# Revit family: Rohrschelle Sigma, M 8, Gummi schwarz
name_source: partatom
category: HLS-Bauteile
revit_build: Autodesk Revit 2017 (Build: 20190507_1515(x64)
units: mm (PartAtom-declared; Revit-internal decimal feet)

## family parameters
Arbeitsebenenbasiert = Ja
Beim Laden mit Abzugskörper schneiden = Nein
Bemaßung runder Anschluss = Durchmesser verwenden
Gemeinsam genutzt = Ja
Immer vertikal = Nein
Raumberechnungspunkt = Nein
Teiletyp = Normal

## types (10) — shared parameters
Anschluss = M8
Anschlußhöhe = 12 mm
Bauart = einteilig
Baustoffklasse = B2
DS = 3 mm  [stored 0.00984252 ft]
DVS = 5 mm  [stored 0.0164042 ft]
Dämmstärke = 3 mm  [stored 0.00984252 ft]
Fabrikat = MEFA
Farbe Schalldämmeinlage = schwarz
Firma = MEFA Befestigungs- und Montagesysteme GmbH
HGA = 8 mm  [stored 0.0262467 ft]
MB = 20 mm  [stored 0.0656168 ft]
Material = Stahl
Material Schalldämmeinlage = EPDM
Materialname = DC01-A, DD11
Mengeneinheit = St
Oberflaeche = galvanisch verzinkt
Schalldämmeinlage = Gummi
Verschluss = Sigma Sicherheits-Schnellverschluss
Verschluss-Schraube = M5
Vorgabe-Ansicht = 1219 mm
max. Temperaturbeständigkeit = 100 °C
max. zul. Last horizontal = 0.00 kN
max. zul. Last vertikal = 0.00 kN
zero-valued in all types: Nennweite DN Rohr, Rohraußendurchmesser, Stärke Material

## per-type parameters (varying)
- Sigma, Ø  6- 10, M 8, Gummi schwarz: A=12 mm  [stored 0.0393701 ft]; Artikelnummer=14510150; B=33 mm  [stored 0.108268 ft]; Breite=33 mm  [stored 0.108268 ft]; D=10 mm  [stored 0.0328084 ft]; D0=16 mm  [stored 0.0524934 ft]; DF1=17 mm; DF2=6 mm  [stored 0.019685 ft]; Dmax=10 mm  [stored 0.0328084 ft]; EAN=4250928454645; Gewicht=0.02 kg; Gewicht pro Bauteil=0.02 kg; H=26 mm  [stored 0.0853018 ft]; Kurztext1=Rohrschelle Sigma 20x1,0; Kurztext2=6 - 10 mm M8 EPDM; MD=1 mm  [stored 0.00328084 ft]; Materialmaße=20x1,0 mm; R=8 mm  [stored 0.0262467 ft]; RM=9 mm  [stored 0.0295276 ft]; Rohraußendurchmesser Zoll=Zoll; max. Höhe=27 mm  [stored 0.0885827 ft]; max. Rohraußendurchmesser=10 mm  [stored 0.0328084 ft]; max. zul. Last=0.60 kN; min. Rohraußendurchmesser=6 mm  [stored 0.019685 ft]; vpe=100 St
- Sigma, Ø 12- 15, M 8, Gummi schwarz: A=12 mm  [stored 0.0393701 ft]; Artikelnummer=14510151; B=41 mm  [stored 0.134514 ft]; Breite=41 mm  [stored 0.134514 ft]; D=15 mm  [stored 0.0492126 ft]; D0=21 mm  [stored 0.0688976 ft]; DF1=19 mm  [stored 0.062336 ft]; DF2=7 mm  [stored 0.0229659 ft]; Dmax=15 mm  [stored 0.0492126 ft]; EAN=4250928432162; Gewicht=0.03 kg; Gewicht pro Bauteil=0.03 kg; H=31 mm  [stored 0.101706 ft]; Kurztext1=Rohrschelle Sigma 20x1,0; Kurztext2=12 - 15 mm M8 EPDM; MD=1 mm  [stored 0.00328084 ft]; Materialmaße=20x1,0 mm; R=11 mm; RM=12 mm  [stored 0.0393701 ft]; Rohraußendurchmesser Zoll=1/4 Zoll; max. Höhe=33 mm  [stored 0.108268 ft]; max. Rohraußendurchmesser=15 mm  [stored 0.0492126 ft]; max. zul. Last=0.60 kN; min. Rohraußendurchmesser=12 mm  [stored 0.0393701 ft]; vpe=100 St
- Sigma, Ø 16- 19, M 8, Gummi schwarz: A=12 mm  [stored 0.0393701 ft]; Artikelnummer=14510191; B=45 mm  [stored 0.147638 ft]; Breite=45 mm  [stored 0.147638 ft]; D=19 mm  [stored 0.062336 ft]; D0=25 mm  [stored 0.082021 ft]; DF1=19 mm  [stored 0.062336 ft]; DF2=7 mm  [stored 0.0229659 ft]; Dmax=19 mm  [stored 0.062336 ft]; EAN=4250928432179; Gewicht=0.03 kg; Gewicht pro Bauteil=0.03 kg; H=35 mm  [stored 0.114829 ft]; Kurztext1=Rohrschelle Sigma 20x1,0; Kurztext2=16 - 19 mm M8 EPDM; MD=1 mm  [stored 0.00328084 ft]; Materialmaße=20x1,0 mm; R=13 mm; RM=14 mm  [stored 0.0459318 ft]; Rohraußendurchmesser Zoll=3/8 Zoll; max. Höhe=37 mm  [stored 0.121391 ft]; max. Rohraußendurchmesser=19 mm  [stored 0.062336 ft]; max. zul. Last=0.60 kN; min. Rohraußendurchmesser=16 mm  [stored 0.0524934 ft]; vpe=100 St
- Sigma, Ø 25- 29, M 8, Gummi schwarz: A=12 mm  [stored 0.0393701 ft]; Artikelnummer=14510291; B=56 mm; Breite=56 mm; D=29 mm  [stored 0.0951444 ft]; D0=35 mm  [stored 0.114829 ft]; DF1=19 mm  [stored 0.062336 ft]; DF2=8 mm  [stored 0.0262467 ft]; Dmax=29 mm  [stored 0.0951444 ft]; EAN=4250928432193; Gewicht=0.04 kg; Gewicht pro Bauteil=0.04 kg; H=45 mm  [stored 0.147638 ft]; Kurztext1=Rohrschelle Sigma 20x1,0; Kurztext2=25 - 29 mm M8 EPDM; MD=1 mm  [stored 0.00328084 ft]; Materialmaße=20x1,0 mm; R=18 mm  [stored 0.0590551 ft]; RM=19 mm  [stored 0.062336 ft]; Rohraußendurchmesser Zoll=3/4 Zoll; max. Höhe=47 mm  [stored 0.154199 ft]; max. Rohraußendurchmesser=29 mm  [stored 0.0951444 ft]; max. zul. Last=0.60 kN; min. Rohraußendurchmesser=25 mm  [stored 0.082021 ft]; vpe=100 St
- Sigma, Ø 32- 35, M 8, Gummi schwarz: A=12 mm  [stored 0.0393701 ft]; Artikelnummer=14510351; B=62 mm; Breite=62 mm; D=35 mm  [stored 0.114829 ft]; D0=41 mm  [stored 0.134514 ft]; DF1=19 mm  [stored 0.062336 ft]; DF2=8 mm  [stored 0.0262467 ft]; Dmax=35 mm  [stored 0.114829 ft]; EAN=4250928432209; Gewicht=0.04 kg; Gewicht pro Bauteil=0.04 kg; H=51 mm; Kurztext1=Rohrschelle Sigma 20x1,0; Kurztext2=32 - 35 mm M8 EPDM; MD=1 mm  [stored 0.00328084 ft]; Materialmaße=20x1,0 mm; R=21 mm  [stored 0.0688976 ft]; RM=22 mm; Rohraußendurchmesser Zoll=1 Zoll; max. Höhe=53 mm; max. Rohraußendurchmesser=35 mm  [stored 0.114829 ft]; max. zul. Last=0.60 kN; min. Rohraußendurchmesser=32 mm  [stored 0.104987 ft]; vpe=100 St
- Sigma, Ø 40- 44, M 8, Gummi schwarz: A=12 mm  [stored 0.0393701 ft]; Artikelnummer=14510441; B=71 mm; Breite=71 mm; D=44 mm  [stored 0.144357 ft]; D0=50 mm  [stored 0.164042 ft]; DF1=19 mm  [stored 0.062336 ft]; DF2=8 mm  [stored 0.0262467 ft]; Dmax=44 mm  [stored 0.144357 ft]; EAN=4250928432216; Gewicht=0.06 kg; Gewicht pro Bauteil=0.06 kg; H=60 mm; Kurztext1=Rohrschelle Sigma 20x1,0; Kurztext2=40 - 44 mm M8 EPDM; MD=1 mm  [stored 0.00328084 ft]; Materialmaße=20x1,0 mm; R=25 mm  [stored 0.082021 ft]; RM=26 mm  [stored 0.0853018 ft]; Rohraußendurchmesser Zoll=1 1/4 Zoll; max. Höhe=62 mm; max. Rohraußendurchmesser=44 mm  [stored 0.144357 ft]; max. zul. Last=0.60 kN; min. Rohraußendurchmesser=40 mm  [stored 0.131234 ft]; vpe=50 St
- Sigma, Ø 48- 52, M 8, Gummi schwarz: A=13 mm; Artikelnummer=14510521; B=80 mm; Breite=80 mm; D=52 mm; D0=58 mm; DF1=20 mm  [stored 0.0656168 ft]; DF2=8 mm  [stored 0.0262467 ft]; Dmax=52 mm; EAN=4250928432223; Gewicht=0.08 kg; Gewicht pro Bauteil=0.08 kg; H=69 mm; Kurztext1=Rohrschelle Sigma 20x1,5; Kurztext2=48 - 52 mm M8 EPDM; MD=2 mm  [stored 0.00656168 ft]; Materialmaße=20x1,5 mm; R=29 mm  [stored 0.0951444 ft]; RM=31 mm  [stored 0.101706 ft]; Rohraußendurchmesser Zoll=1 1/2 Zoll; max. Höhe=70 mm; max. Rohraußendurchmesser=52 mm; max. zul. Last=1.10 kN; min. Rohraußendurchmesser=48 mm  [stored 0.15748 ft]; vpe=50 St
- Sigma, Ø 20- 23, M 8, Gummi schwarz: A=12 mm  [stored 0.0393701 ft]; Artikelnummer=14510231; B=51 mm; Breite=51 mm; D=23 mm  [stored 0.0754593 ft]; D0=29 mm  [stored 0.0951444 ft]; DF1=20 mm  [stored 0.0656168 ft]; DF2=8 mm  [stored 0.0262467 ft]; Dmax=23 mm  [stored 0.0754593 ft]; EAN=4250928432186; Gewicht=0.03 kg; Gewicht pro Bauteil=0.03 kg; H=39 mm  [stored 0.127953 ft]; Kurztext1=Rohrschelle Sigma 20x1,0; Kurztext2=20 - 23 mm M8 EPDM; MD=1 mm  [stored 0.00328084 ft]; Materialmaße=20x1,0 mm; R=15 mm  [stored 0.0492126 ft]; RM=16 mm  [stored 0.0524934 ft]; Rohraußendurchmesser Zoll=1/2 Zoll; max. Höhe=41 mm  [stored 0.134514 ft]; max. Rohraußendurchmesser=23 mm  [stored 0.0754593 ft]; max. zul. Last=0.60 kN; min. Rohraußendurchmesser=20 mm  [stored 0.0656168 ft]; vpe=100 St
- Sigma, Ø 53- 57, M 8, Gummi schwarz: A=13 mm; Artikelnummer=14510571; B=85 mm; Breite=85 mm; D=57 mm; D0=63 mm; DF1=20 mm  [stored 0.0656168 ft]; DF2=8 mm  [stored 0.0262467 ft]; Dmax=57 mm; EAN=4250928432230; Gewicht=0.09 kg; Gewicht pro Bauteil=0.09 kg; H=74 mm; Kurztext1=Rohrschelle Sigma 20x1,5; Kurztext2=53 - 57 mm M8 EPDM; MD=2 mm  [stored 0.00656168 ft]; Materialmaße=20x1,5 mm; R=32 mm  [stored 0.104987 ft]; RM=33 mm  [stored 0.108268 ft]; Rohraußendurchmesser Zoll=Zoll; max. Höhe=75 mm; max. Rohraußendurchmesser=57 mm; max. zul. Last=1.10 kN; min. Rohraußendurchmesser=53 mm; vpe=50 St
- Sigma, Ø 58- 60, M 8, Gummi schwarz: A=13 mm; Artikelnummer=14510601; B=89 mm; Breite=89 mm; D=60 mm; D0=66 mm; DF1=21 mm  [stored 0.0688976 ft]; DF2=8 mm  [stored 0.0262467 ft]; Dmax=60 mm; EAN=4250928432247; Gewicht=0.09 kg; Gewicht pro Bauteil=0.09 kg; H=77 mm; Kurztext1=Rohrschelle Sigma 20x1,5; Kurztext2=58 - 60 mm M8 EPDM; MD=2 mm  [stored 0.00656168 ft]; Materialmaße=20x1,5 mm; R=33 mm  [stored 0.108268 ft]; RM=35 mm  [stored 0.114829 ft]; Rohraußendurchmesser Zoll=2 Zoll; max. Höhe=79 mm; max. Rohraußendurchmesser=60 mm; max. zul. Last=1.10 kN; min. Rohraußendurchmesser=58 mm; vpe=50 St

note: [stored X ft] marks values corroborated as IEEE doubles in the binary element streams (Revit-internal decimal feet)

## geometry (parser evidence)
native form markers: Sweep x3
no freeform markers — native parametric forms only
